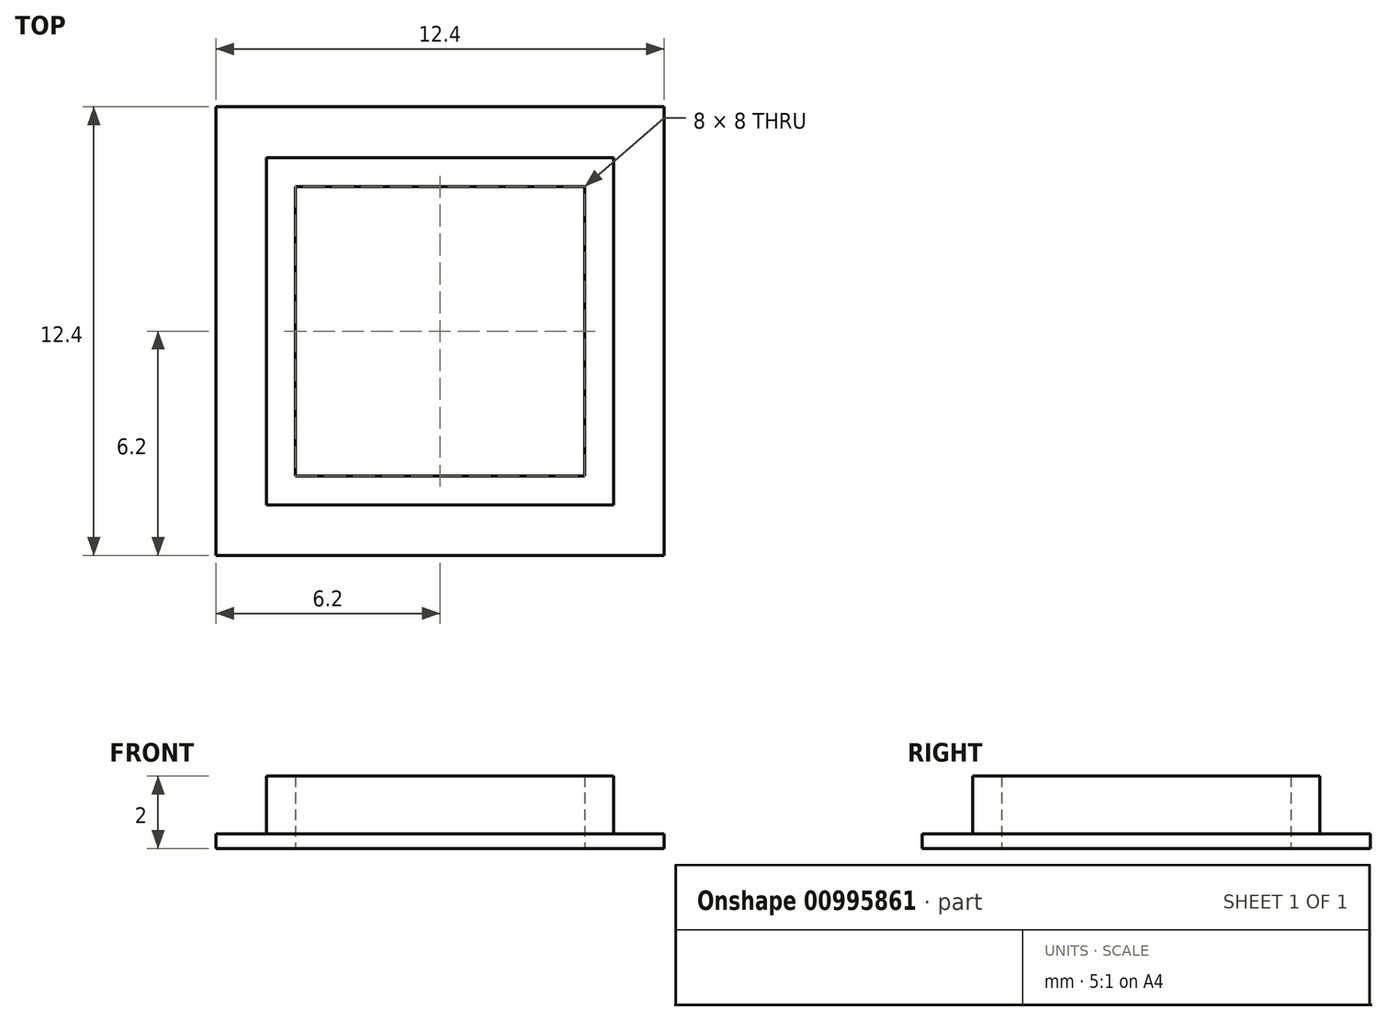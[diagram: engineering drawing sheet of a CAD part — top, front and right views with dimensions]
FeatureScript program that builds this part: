
annotation { "Feature Type Name" : "Feature", "Feature Type Description" : "" }
export const myFeature = defineFeature(function(context is Context, id is Id, definition is map)
    precondition{}
    {
        {
            var Q0;
            Q0=qCreatedBy(makeId("Top.planeOp"),FACE);
            var sketch = newSketch(context, id + "F0", { "sketchPlane" : qUnion([Q0])});
            skLineSegment(sketch, "E0.bottom", {"start": v(4.8, -4.8) * mm, "end": v(-4.8, -4.8) * mm});
            skLineSegment(sketch, "E0.top", {"start": v(4.8, 4.8) * mm, "end": v(-4.8, 4.8) * mm});
            skLineSegment(sketch, "E0.left", {"start": v(4.8, -4.8) * mm, "end": v(4.8, 4.8) * mm});
            skLineSegment(sketch, "E0.right", {"start": v(-4.8, -4.8) * mm, "end": v(-4.8, 4.8) * mm});
            skPoint(sketch, "E0.middle", {"position": v(0, 0) * mm});
            skLineSegment(sketch, "E1.bottom", {"start": v(6.2, 6.2) * mm, "end": v(-6.2, 6.2) * mm});
            skLineSegment(sketch, "E1.top", {"start": v(6.2, -6.2) * mm, "end": v(-6.2, -6.2) * mm});
            skLineSegment(sketch, "E1.left", {"start": v(6.2, 6.2) * mm, "end": v(6.2, -6.2) * mm});
            skLineSegment(sketch, "E1.right", {"start": v(-6.2, 6.2) * mm, "end": v(-6.2, -6.2) * mm});
            skSolve(sketch);
        }
        {
            var Q0;
            Q0=makeQuery(id+"F0.imprint","IMPRINT",FACE,{"disambiguationData":[TD([[makeQuery(id+"F0.imprint","IMPRINT",EDGE,{"derivedFrom":sQuery(id+"F0.wireOp",EDGE,"E0.bottom")}),-1.0]])]});
            extrude(context, id + "F1", {"entities" : qUnion([Q0]), "depth" : 2 * mm, "offsetDistance" : 25 * mm});
        }
        {
            var Q0;
            Q0=makeQuery(id+"F1.opExtrude","CAP_FACE",FACE,{"disambiguationData":[OSD([sQuery(id+"F0.wireOp",EDGE,"E0.bottom"),sQuery(id+"F0.wireOp",EDGE,"E0.top"),sQuery(id+"F0.wireOp",EDGE,"E0.left"),sQuery(id+"F0.wireOp",EDGE,"E0.right")])],"isStart":false});
            shell(context, id + "F2", {"entities" : qUnion([Q0]), "thickness" : .8 * mm});
        }
        {
            var Q0;
            Q0=makeQuery(id+"F0.imprint","IMPRINT",FACE,{"disambiguationData":[TD([[makeQuery(id+"F0.imprint","IMPRINT",EDGE,{"derivedFrom":sQuery(id+"F0.wireOp",EDGE,"E0.bottom")}),1.0]])]});
            extrude(context, id + "F3", {"entities" : qUnion([Q0]), "operationType" : NewBodyOperationType.ADD, "depth" : .4 * mm, "offsetDistance" : 25 * mm});
        }
        {
            var Q0;
            Q0=makeQuery(id+"F2.opShell","OFFSET_FACE",FACE,{"disambiguationData":[OSD([sQuery(id+"F0.wireOp",EDGE,"E0.bottom"),sQuery(id+"F0.wireOp",EDGE,"E0.top"),sQuery(id+"F0.wireOp",EDGE,"E0.left"),sQuery(id+"F0.wireOp",EDGE,"E0.right")])]});
            extrude(context, id + "F4", {"entities" : qUnion([Q0]), "operationType" : NewBodyOperationType.REMOVE, "oppositeDirection" : true, "depth" : 1 * mm, "offsetDistance" : 25 * mm});
        }
    });
